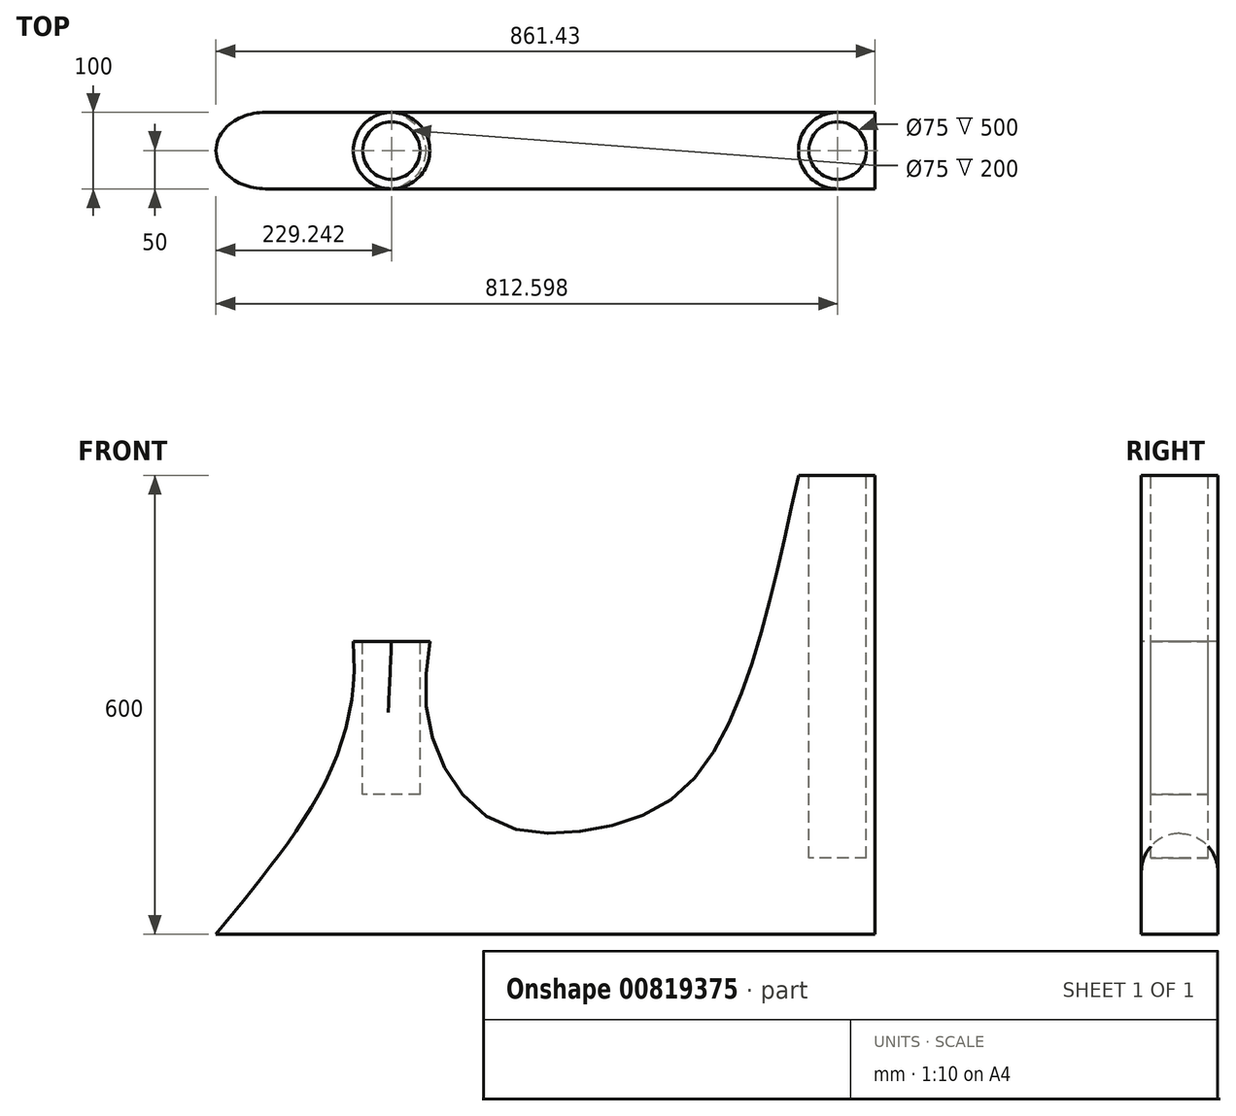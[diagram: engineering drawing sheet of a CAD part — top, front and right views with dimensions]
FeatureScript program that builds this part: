
annotation { "Feature Type Name" : "Feature", "Feature Type Description" : "" }
export const myFeature = defineFeature(function(context is Context, id is Id, definition is map)
    precondition{}
    {
        {
            var Q0;
            Q0=qCreatedBy(makeId("Front.planeOp"),FACE);
            var sketch = newSketch(context, id + "F0", { "sketchPlane" : qUnion([Q0])});
            skLineSegment(sketch, "E0", {"start": v(-52.65, -51.95) * mm, "end": v(47.35, -51.95) * mm});
            skLineSegment(sketch, "E1", {"start": v(47.35, -51.95) * mm, "end": v(1045.23, -51.95) * mm, "construction": true});
            skLineSegment(sketch, "E2", {"start": v(1045.23, -51.95) * mm, "end": v(1045.23, 539.6) * mm, "construction": true});
            skFitSpline(sketch, "E3", {"points": [v(-52.65, -51.95) * mm, v(91, 148.63) * mm, v(126.76, 272.19) * mm, v(126.76, 330.71) * mm], "startDerivative": vector(371.6, 452.87) * mm, "endDerivative": vector(-14.15, 244.2) * mm});
            skLineSegment(sketch, "E4", {"start": v(126.76, 330.71) * mm, "end": v(226.76, 330.71) * mm});
            skFitSpline(sketch, "E5", {"points": [v(226.76, 330.71) * mm, v(226.76, 216.91) * mm, v(303.97, 99.86) * mm, v(429.15, 83.6) * mm, v(575.47, 155.13) * mm, v(708.78, 548.05) * mm], "startDerivative": vector(-91.1, -691.5) * mm, "endDerivative": vector(335.95, 1544.03) * mm});
            skLineSegment(sketch, "E6", {"start": v(708.78, 548.05) * mm, "end": v(808.78, 548.05) * mm});
            skLineSegment(sketch, "E7", {"start": v(808.78, 548.05) * mm, "end": v(808.78, -51.95) * mm});
            skLineSegment(sketch, "E8", {"start": v(808.78, -51.95) * mm, "end": v(47.35, -51.95) * mm});
            skSolve(sketch);
        }
        {
            var Q0;
            Q0=makeQuery(id+"F0.imprint","IMPRINT",FACE,{"disambiguationData":[TD([[makeQuery(id+"F0.imprint","IMPRINT",EDGE,{"derivedFrom":sQuery(id+"F0.wireOp",EDGE,"E0")}),1.0]])]});
            extrude(context, id + "F1", {"entities" : qUnion([Q0]), "endBound" : BoundingType.SYMMETRIC, "depth" : 100 * mm, "offsetDistance" : 25 * mm});
        }
        {
            var Q0;
            Q0=makeQuery(id+"F1.opExtrude","CAP_EDGE",EDGE,{"disambiguationData":[OSD([sQuery(id+"F0.wireOp",EDGE,"E5")])],"isStart":false});
            var Q1;
            Q1=makeQuery(id+"F1.opExtrude","CAP_EDGE",EDGE,{"disambiguationData":[OSD([sQuery(id+"F0.wireOp",EDGE,"E5")])],"isStart":true});
            var Q2;
            Q2=makeQuery(id+"F1.opExtrude","CAP_EDGE",EDGE,{"disambiguationData":[OSD([sQuery(id+"F0.wireOp",EDGE,"E3")])],"isStart":true});
            var Q3;
            Q3=makeQuery(id+"F1.opExtrude","CAP_EDGE",EDGE,{"disambiguationData":[OSD([sQuery(id+"F0.wireOp",EDGE,"E3")])],"isStart":false});
            fillet(context, id + "F2", {"entities" : qUnion([Q0, Q1, Q2, Q3]), "radius" : 50 * mm, "tangentPropagation" : true, "allowEdgeOverflow" : false});
        }
        {
            var Q0;
            Q0=makeQuery(id+"F1.opExtrude","SWEPT_FACE",FACE,{"disambiguationData":[OSD([sQuery(id+"F0.wireOp",EDGE,"E6")])]});
            var sketch = newSketch(context, id + "F3", { "sketchPlane" : qUnion([Q0])});
            skCircle(sketch, "E9", {"center": v(759.95, 0) * mm, "radius": 37.5 * mm});
            skSolve(sketch);
        }
        {
            var Q0;
            Q0 = qSketchRegion(id + "F3", true);
            extrude(context, id + "F4", {"entities" : qUnion([Q0]), "operationType" : NewBodyOperationType.REMOVE, "oppositeDirection" : true, "depth" : 500 * mm, "offsetDistance" : 25 * mm});
        }
        {
            var Q0;
            Q0=makeQuery(id+"F1.opExtrude","SWEPT_FACE",FACE,{"disambiguationData":[OSD([sQuery(id+"F0.wireOp",EDGE,"E4")])]});
            var sketch = newSketch(context, id + "F5", { "sketchPlane" : qUnion([Q0])});
            skCircle(sketch, "E10", {"center": v(176.6, 0) * mm, "radius": 37.5 * mm});
            skSolve(sketch);
        }
        {
            var Q0;
            Q0 = qSketchRegion(id + "F5", true);
            extrude(context, id + "F6", {"entities" : qUnion([Q0]), "operationType" : NewBodyOperationType.REMOVE, "oppositeDirection" : true, "depth" : 200 * mm, "offsetDistance" : 25 * mm});
        }
    });
